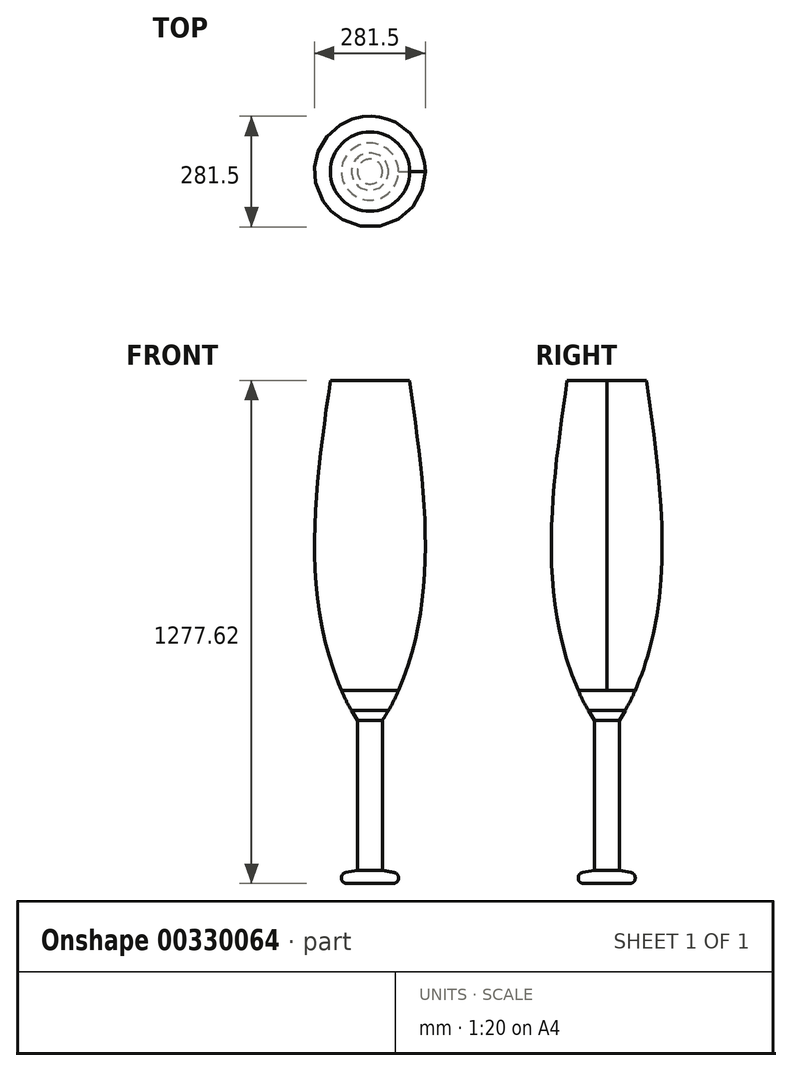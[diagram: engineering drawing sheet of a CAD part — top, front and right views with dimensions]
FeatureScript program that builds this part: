
annotation { "Feature Type Name" : "Feature", "Feature Type Description" : "" }
export const myFeature = defineFeature(function(context is Context, id is Id, definition is map)
    precondition{}
    {
        {
            var Q0;
            Q0=qCreatedBy(makeId("Top.planeOp"),FACE);
            cPlane(context, id + "F0", {"entities" : qUnion([Q0]), "cplaneType" : CPlaneType.OFFSET, "offset" : 25.4 * mm, "oppositeDirection" : true, "width" : 152.4 * mm, "height" : 152.4 * mm});
        }
        {
            var Q0;
            Q0=qCreatedBy(id+"F0.planeOp",FACE);
            var sketch = newSketch(context, id + "F1", { "sketchPlane" : qUnion([Q0])});
            skCircle(sketch, "E0", {"center": v(0, 0) * mm, "radius": 72.4 * mm});
            skSolve(sketch);
        }
        {
            var Q0;
            Q0=qCreatedBy(makeId("Top.planeOp"),FACE);
            var sketch = newSketch(context, id + "F2", { "sketchPlane" : qUnion([Q0])});
            skCircle(sketch, "E1", {"center": v(0, 0) * mm, "radius": 72.4 * mm});
            skSolve(sketch);
        }
        {
            var Q0;
            Q0=qCreatedBy(makeId("Top.planeOp"),FACE);
            cPlane(context, id + "F3", {"entities" : qUnion([Q0]), "cplaneType" : CPlaneType.OFFSET, "offset" : 7.62 * mm, "width" : 152.4 * mm, "height" : 152.4 * mm});
        }
        {
            var Q0;
            Q0=qCreatedBy(id+"F3.planeOp",FACE);
            var sketch = newSketch(context, id + "F4", { "sketchPlane" : qUnion([Q0])});
            skCircle(sketch, "E2", {"center": v(0, 0) * mm, "radius": 31.75 * mm});
            skSolve(sketch);
        }
        {
            var Q0;
            Q0=makeQuery(id+"F2.imprint","IMPRINT",FACE,{"disambiguationData":[TD([[makeQuery(id+"F2.imprint","IMPRINT",EDGE,{"derivedFrom":sQuery(id+"F2.wireOp",EDGE,"E1")}),1.0]])]});
            var Q1;
            Q1=makeQuery(id+"F4.imprint","IMPRINT",FACE,{"disambiguationData":[TD([[makeQuery(id+"F4.imprint","IMPRINT",EDGE,{"derivedFrom":sQuery(id+"F4.wireOp",EDGE,"E2")}),1.0]])]});
            loft(context, id + "F5", {"sheetProfilesArray" : [{ "sheetProfileEntities" : qUnion([Q0]) }, { "sheetProfileEntities" : qUnion([Q1]) }]});
        }
        {
            var Q0;
            Q0=makeQuery(id+"F4.imprint","IMPRINT",FACE,{"disambiguationData":[TD([[makeQuery(id+"F4.imprint","IMPRINT",EDGE,{"derivedFrom":sQuery(id+"F4.wireOp",EDGE,"E2")}),1.0]])]});
            extrude(context, id + "F6", {"entities" : qUnion([Q0]), "operationType" : NewBodyOperationType.ADD, "depth" : 381 * mm});
        }
        {
            var Q1;
            Q1=makeQuery(id+"F2.imprint","IMPRINT",FACE,{"disambiguationData":[TD([[makeQuery(id+"F2.imprint","IMPRINT",EDGE,{"derivedFrom":sQuery(id+"F2.wireOp",EDGE,"E1")}),1.0]])]});
            var Q2;
            Q2=makeQuery(id+"F1.imprint","IMPRINT",FACE,{"disambiguationData":[TD([[makeQuery(id+"F1.imprint","IMPRINT",EDGE,{"derivedFrom":sQuery(id+"F1.wireOp",EDGE,"E0")}),1.0]])]});
            loft(context, id + "F7", {"operationType" : NewBodyOperationType.ADD, "sheetProfilesArray" : [{ "sheetProfileEntities" : qUnion([Q1]) }, { "sheetProfileEntities" : qUnion([Q2]) }]});
        }
        {
            var Q0;
            Q0=makeQuery(id+"F6.opExtrude","CAP_FACE",FACE,{"disambiguationData":[OSD([sQuery(id+"F4.wireOp",EDGE,"E2")])],"isStart":false});
            cPlane(context, id + "F8", {"entities" : qUnion([Q0]), "cplaneType" : CPlaneType.OFFSET, "offset" : 25.4 * mm, "width" : 152.4 * mm, "height" : 152.4 * mm});
        }
        {
            var Q0;
            Q0=qCreatedBy(id+"F8.planeOp",FACE);
            var sketch = newSketch(context, id + "F9", { "sketchPlane" : qUnion([Q0])});
            skCircle(sketch, "E3", {"center": v(0, 0) * mm, "radius": 47 * mm});
            skSolve(sketch);
        }
        {
            var Q1;
            Q1=makeQuery(id+"F6.opExtrude","CAP_FACE",FACE,{"disambiguationData":[OSD([sQuery(id+"F4.wireOp",EDGE,"E2")])],"isStart":false});
            var Q2;
            Q2=makeQuery(id+"F9.imprint","IMPRINT",FACE,{"disambiguationData":[TD([[makeQuery(id+"F9.imprint","IMPRINT",EDGE,{"derivedFrom":sQuery(id+"F9.wireOp",EDGE,"E3")}),1.0]])]});
            loft(context, id + "F10", {"operationType" : NewBodyOperationType.ADD, "sheetProfilesArray" : [{ "sheetProfileEntities" : qUnion([Q1]) }, { "sheetProfileEntities" : qUnion([Q2]) }]});
        }
        {
            var Q0;
            Q0=makeQuery(id+"F10.opLoft","CAP_FACE",FACE,{"disambiguationData":[OSD([makeQuery(id+"F9.imprint","IMPRINT",FACE,{"disambiguationData":[TD([[makeQuery(id+"F9.imprint","IMPRINT",EDGE,{"derivedFrom":sQuery(id+"F9.wireOp",EDGE,"E3")}),1.0]])]})])],"isStart":true});
            cPlane(context, id + "F11", {"entities" : qUnion([Q0]), "cplaneType" : CPlaneType.OFFSET, "offset" : 25.4 * mm, "width" : 152.4 * mm, "height" : 152.4 * mm});
        }
        {
            var Q0;
            Q0=qCreatedBy(id+"F11.planeOp",FACE);
            var sketch = newSketch(context, id + "F12", { "sketchPlane" : qUnion([Q0])});
            skCircle(sketch, "E4", {"center": v(0, 0) * mm, "radius": 60.96 * mm});
            skSolve(sketch);
        }
        {
            var Q0;
            Q0=makeQuery(id+"F12.imprint","IMPRINT",FACE,{"disambiguationData":[TD([[makeQuery(id+"F12.imprint","IMPRINT",EDGE,{"derivedFrom":sQuery(id+"F12.wireOp",EDGE,"E4")}),1.0]])]});
            cPlane(context, id + "F13", {"entities" : qUnion([Q0]), "cplaneType" : CPlaneType.OFFSET, "offset" : 25.4 * mm, "width" : 152.4 * mm, "height" : 152.4 * mm});
        }
        {
            var Q0;
            Q0=qCreatedBy(id+"F13.planeOp",FACE);
            var sketch = newSketch(context, id + "F14", { "sketchPlane" : qUnion([Q0])});
            skCircle(sketch, "E5", {"center": v(0, 0) * mm, "radius": 72.4 * mm});
            skSolve(sketch);
        }
        {
            var Q0;
            Q0=makeQuery(id+"F10.opLoft","CAP_FACE",FACE,{"disambiguationData":[OSD([makeQuery(id+"F9.imprint","IMPRINT",FACE,{"disambiguationData":[TD([[makeQuery(id+"F9.imprint","IMPRINT",EDGE,{"derivedFrom":sQuery(id+"F9.wireOp",EDGE,"E3")}),1.0]])]})])],"isStart":true});
            var Q1;
            Q1=makeQuery(id+"F12.imprint","IMPRINT",FACE,{"disambiguationData":[TD([[makeQuery(id+"F12.imprint","IMPRINT",EDGE,{"derivedFrom":sQuery(id+"F12.wireOp",EDGE,"E4")}),1.0]])]});
            var Q2;
            Q2=makeQuery(id+"F14.imprint","IMPRINT",FACE,{"disambiguationData":[TD([[makeQuery(id+"F14.imprint","IMPRINT",EDGE,{"derivedFrom":sQuery(id+"F14.wireOp",EDGE,"E5")}),1.0]])]});
            loft(context, id + "F15", {"sheetProfilesArray" : [{ "sheetProfileEntities" : qUnion([Q0]) }, { "sheetProfileEntities" : qUnion([Q1]) }, { "sheetProfileEntities" : qUnion([Q2]) }]});
        }
        {
            var Q0;
            Q0=makeQuery(id+"FFG5y7JXaVTRDyw_2.opExtrude","CAP_EDGE",EDGE,{"disambiguationData":[OSD([sQuery(id+"F4.wireOp",EDGE,"E2"),sQuery(id+"F9.wireOp",EDGE,"E3"),sQuery(id+"F14.wireOp",EDGE,"E5")])],"isStart":false});
            var Q1;
            Q1=makeQuery(id+"F7.opLoft","MID_CAP_EDGE",EDGE,{"disambiguationData":[OSD([sQuery(id+"F1.wireOp",EDGE,"E0"),sQuery(id+"F2.wireOp",EDGE,"E1")])],"capPos":1.0});
            var Q2;
            {var subQ0=sQuery(id+"F2.wireOp",EDGE,"E1");Q2=makeQuery(id+"F7.boolean.opBoolean","MERGE",EDGE,{"derivedFrom":[makeQuery(id+"F5.opLoft","MID_CAP_EDGE",EDGE,{"disambiguationData":[OSD([subQ0])],"capPos":0.0}),makeQuery(id+"F7.opLoft","MID_CAP_EDGE",EDGE,{"disambiguationData":[OSD([subQ0])],"capPos":0.0})]});}
            fillet(context, id + "F16", {"entities" : qUnion([Q0, Q1, Q2]), "radius" : 12.7 * mm, "tangentPropagation" : true, "allowEdgeOverflow" : false});
        }
        {
            var Q0;
            Q0=makeQuery(id+"F15.opLoft","CAP_FACE",FACE,{"disambiguationData":[OSD([makeQuery(id+"F14.imprint","IMPRINT",FACE,{"disambiguationData":[TD([[makeQuery(id+"F14.imprint","IMPRINT",EDGE,{"derivedFrom":sQuery(id+"F14.wireOp",EDGE,"E5")}),1.0]])]})])],"isStart":true});
            cPlane(context, id + "F17", {"entities" : qUnion([Q0]), "cplaneType" : CPlaneType.OFFSET, "offset" : 25.4 * mm, "width" : 152.4 * mm, "height" : 152.4 * mm});
        }
        {
            var Q0;
            Q0=qCreatedBy(id+"F17.planeOp",FACE);
            cPlane(context, id + "F18", {"entities" : qUnion([Q0]), "cplaneType" : CPlaneType.OFFSET, "offset" : 762 * mm, "width" : 152.4 * mm, "height" : 152.4 * mm});
        }
        {
            var Q0;
            Q0=qCreatedBy(id+"F17.planeOp",FACE);
            var sketch = newSketch(context, id + "F19", { "sketchPlane" : qUnion([Q0])});
            skCircle(sketch, "E6", {"center": v(0, 0) * mm, "radius": 82.73 * mm});
            skSolve(sketch);
        }
        {
            var Q0;
            Q0=qCreatedBy(id+"F18.planeOp",FACE);
            var sketch = newSketch(context, id + "F20", { "sketchPlane" : qUnion([Q0])});
            skCircle(sketch, "E7", {"center": v(0, 0) * mm, "radius": 100.7 * mm});
            skSolve(sketch);
        }
        {
            var Q1;
            Q1=makeQuery(id+"F15.opLoft","CAP_FACE",FACE,{"disambiguationData":[OSD([makeQuery(id+"F14.imprint","IMPRINT",FACE,{"disambiguationData":[TD([[makeQuery(id+"F14.imprint","IMPRINT",EDGE,{"derivedFrom":sQuery(id+"F14.wireOp",EDGE,"E5")}),1.0]])]})])],"isStart":true});
            var Q2;
            Q2=makeQuery(id+"F19.imprint","IMPRINT",FACE,{"disambiguationData":[TD([[makeQuery(id+"F19.imprint","IMPRINT",EDGE,{"derivedFrom":sQuery(id+"F19.wireOp",EDGE,"E6")}),1.0]])]});
            var Q3;
            Q3=makeQuery(id+"F20.imprint","IMPRINT",FACE,{"disambiguationData":[TD([[makeQuery(id+"F20.imprint","IMPRINT",EDGE,{"derivedFrom":sQuery(id+"F20.wireOp",EDGE,"E7")}),1.0]])]});
            loft(context, id + "F21", {"operationType" : NewBodyOperationType.ADD, "sheetProfilesArray" : [{ "sheetProfileEntities" : qUnion([Q1]) }, { "sheetProfileEntities" : qUnion([Q2]) }, { "sheetProfileEntities" : qUnion([Q3]) }]});
        }
    });
